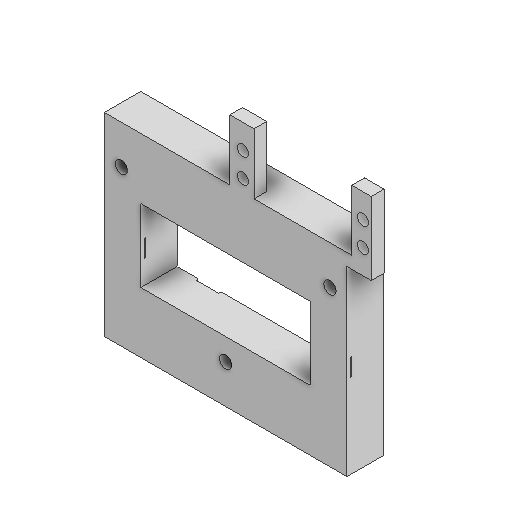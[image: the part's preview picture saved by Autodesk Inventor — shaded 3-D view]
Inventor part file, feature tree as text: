
AUTODESK INVENTOR PART (.ipt)
format: ipt  version: 2025.1 (Build 291241000, 241)  size: 255,488 bytes
history: native  units: mm
features: sketch x12, extrude x10, hole x2, chamfer x1
ambient origin geometry x8: Origin, YZ Plane, XZ Plane, XY Plane, X Axis, Y Axis, Z Axis, Center Point
bodies: Body1 (feature_tree)
feature tree (25):
  extrude  "Wyciągnięcie proste4"  Depth=100.0mm
  extrude  "Wyciągnięcie proste5"  Depth=80.0mm
  extrude  "Wyciągnięcie proste6"  Depth=70.0mm
  extrude  "Wyciągnięcie proste7"  Depth=50.0mm
  hole  "Otwór2"  [1 undecoded]
  extrude  "Wyciągnięcie proste8"  Depth=2.0mm TaperAngle=0.0deg
  chamfer  "Faza2"  Distance=0.5mm
  extrude  "Wyciągnięcie proste9"  Depth=7.0mm
  extrude  "Wyciągnięcie proste10"  Depth=1.5mm
  extrude  "Wyciągnięcie proste11"  Depth=41.741mm
  hole  "Otwór3"  [1 undecoded]
  extrude  "Wyciągnięcie proste12"  Depth=10.0mm TaperAngle=0.0deg
  extrude  "Wyciągnięcie proste13"  Depth=16.0mm
  sketch  "Szkic5"
  sketch  "Szkic6"
  sketch  "Szkic7"
  sketch  "Szkic8"
  sketch  "Szkic9"
  sketch  "Szkic10"
  sketch  "Szkic11"
  sketch  "Szkic12"
  sketch  "Szkic14"
  sketch  "Szkic15"
  sketch  "Szkic16"
  sketch  "Szkic17"
note: 2 required parameter values undecoded (feature->parameter linkage not recoverable at this tier; creation-order binding heuristic only, values carry confidence <= 0.55)
